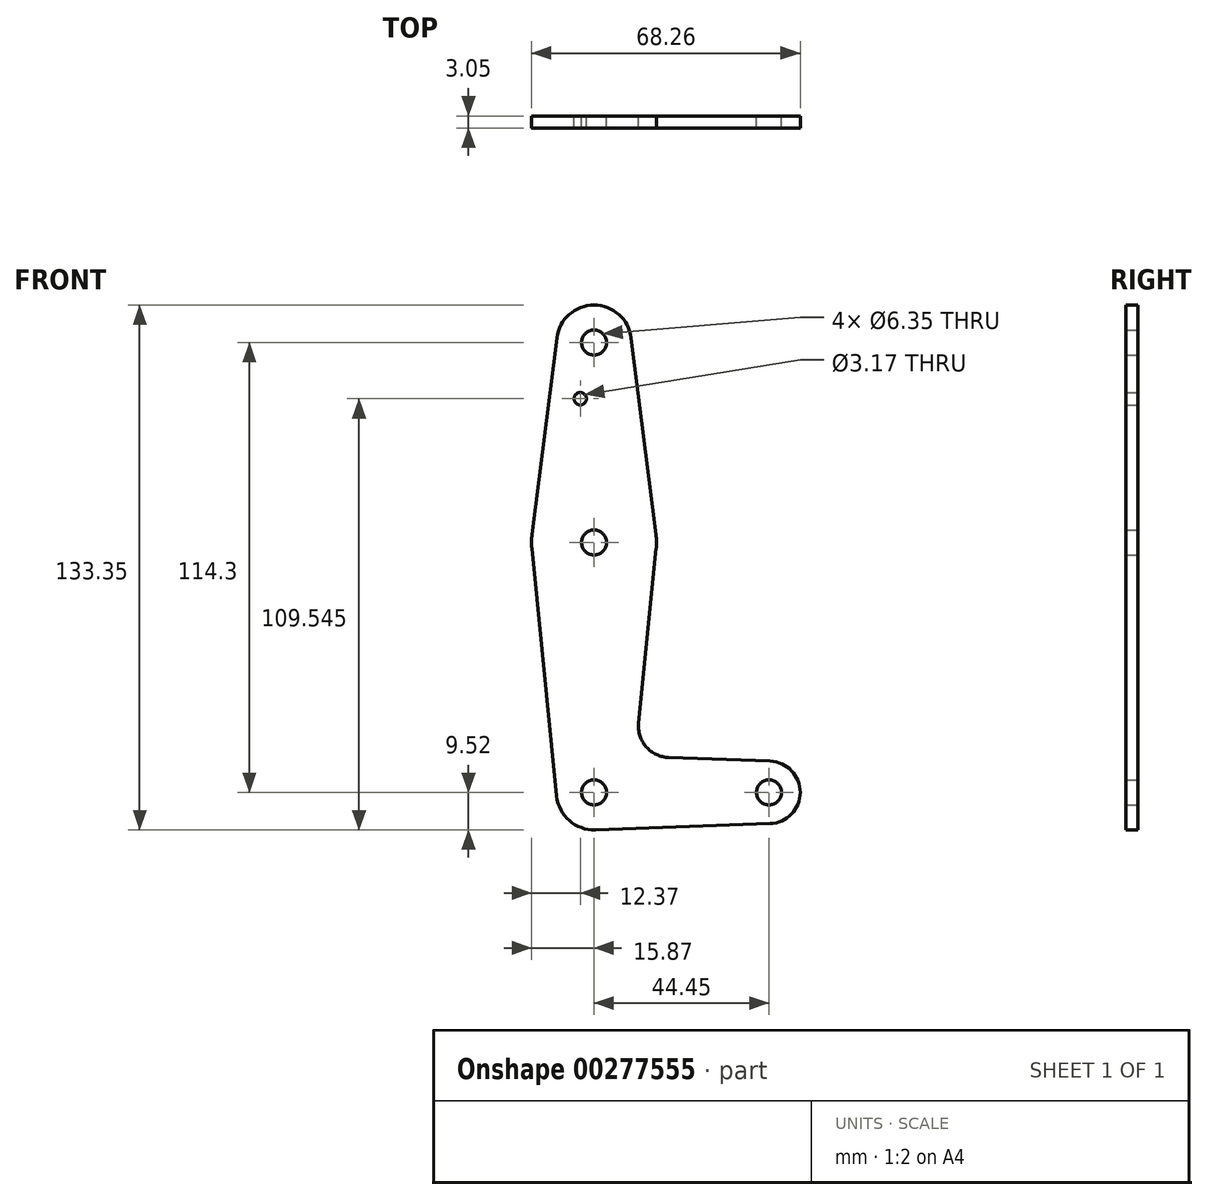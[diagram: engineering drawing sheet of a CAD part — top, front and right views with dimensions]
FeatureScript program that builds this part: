
annotation { "Feature Type Name" : "Feature", "Feature Type Description" : "" }
export const myFeature = defineFeature(function(context is Context, id is Id, definition is map)
    precondition{}
    {
        {
            var Q0;
            Q0=qCreatedBy(makeId("Front.planeOp"),FACE);
            var sketch = newSketch(context, id + "F0", { "sketchPlane" : qUnion([Q0])});
            skLineSegment(sketch, "E0", {"start": v(0, 0) * mm, "end": v(44.45, 0) * mm, "construction": true});
            skLineSegment(sketch, "E1", {"start": v(0, 0) * mm, "end": v(0, 114.3) * mm, "construction": true});
            skCircle(sketch, "E2", {"center": v(0, 114.3) * mm, "radius": 9.53 * mm});
            skCircle(sketch, "E3", {"center": v(44.45, 0) * mm, "radius": 7.94 * mm});
            skCircle(sketch, "E4", {"center": v(0, 0) * mm, "radius": 9.53 * mm});
            skCircle(sketch, "E5", {"center": v(0, 63.5) * mm, "radius": 15.88 * mm});
            skLineSegment(sketch, "E6", {"start": v(-15.75, 65.48) * mm, "end": v(-9.45, 115.5) * mm});
            skLineSegment(sketch, "E7", {"start": v(15.75, 65.48) * mm, "end": v(9.45, 115.5) * mm});
            skLineSegment(sketch, "E8", {"start": v(18.97, 8.85) * mm, "end": v(44.73, 7.93) * mm});
            skLineSegment(sketch, "E9", {"start": v(0.34, -9.52) * mm, "end": v(44.73, -7.93) * mm});
            skLineSegment(sketch, "E10", {"start": v(15.8, 61.91) * mm, "end": v(11.34, 17.6) * mm});
            skLineSegment(sketch, "E11", {"start": v(-15.8, 61.91) * mm, "end": v(-9.48, -0.95) * mm});
            skCircle(sketch, "E12", {"center": v(0, 63.5) * mm, "radius": 3.18 * mm});
            skCircle(sketch, "E13", {"center": v(0, 114.3) * mm, "radius": 3.18 * mm});
            skCircle(sketch, "E14", {"center": v(0, 0) * mm, "radius": 3.18 * mm});
            skCircle(sketch, "E15", {"center": v(44.45, 0) * mm, "radius": 3.18 * mm});
            skArc(sketch, "E16.filletArc", {"start": v(11.34, 17.6) * mm, "mid": v(13.26, 11.57) * mm, "end": v(18.97, 8.85) * mm});
            skCircle(sketch, "E17", {"center": v(-3.5, 100.03) * mm, "radius": 1.59 * mm});
            skSolve(sketch);
        }
        {
            var Q0;
            {var subQ1=sQuery(id+"F0.wireOp",EDGE,"E6");Q0=makeQuery(id+"F0.imprint","IMPRINT",FACE,{"disambiguationData":[TD([[makeQuery(id+"F0.imprint","IMPRINT",EDGE,{"derivedFrom":subQ1}),-1.0]])]});}
            var Q1;
            Q1=makeQuery(id+"F0.imprint","IMPRINT",FACE,{"disambiguationData":[TD([[makeQuery(id+"F0.imprint","IMPRINT",EDGE,{"derivedFrom":sQuery(id+"F0.wireOp",EDGE,"E13")}),-1.0]])]});
            var Q2;
            Q2=makeQuery(id+"F0.imprint","IMPRINT",FACE,{"disambiguationData":[TD([[makeQuery(id+"F0.imprint","IMPRINT",EDGE,{"derivedFrom":sQuery(id+"F0.wireOp",EDGE,"E12")}),-1.0]])]});
            var Q3;
            {var subQ0=sQuery(id+"F0.wireOp",EDGE,"E8");Q3=makeQuery(id+"F0.imprint","IMPRINT",FACE,{"disambiguationData":[TD([[makeQuery(id+"F0.imprint","IMPRINT",EDGE,{"derivedFrom":subQ0}),-1.0]])]});}
            var Q4;
            Q4=makeQuery(id+"F0.imprint","IMPRINT",FACE,{"disambiguationData":[TD([[makeQuery(id+"F0.imprint","IMPRINT",EDGE,{"derivedFrom":sQuery(id+"F0.wireOp",EDGE,"E14")}),-1.0]])]});
            var Q5;
            Q5=makeQuery(id+"F0.imprint","IMPRINT",FACE,{"disambiguationData":[TD([[makeQuery(id+"F0.imprint","IMPRINT",EDGE,{"derivedFrom":sQuery(id+"F0.wireOp",EDGE,"E15")}),-1.0]])]});
            extrude(context, id + "F1", {"entities" : qUnion([Q0, Q1, Q2, Q3, Q4, Q5]), "depth" : 3.05 * mm});
        }
    });
